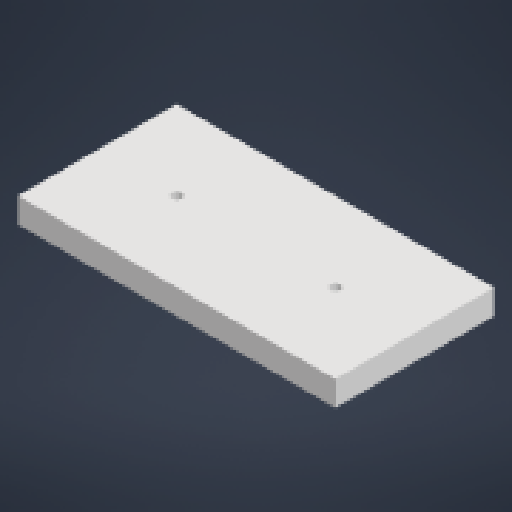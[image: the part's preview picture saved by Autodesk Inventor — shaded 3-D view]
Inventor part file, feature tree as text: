
AUTODESK INVENTOR PART (.ipt)
format: ipt  version: 2023 (Build 270158000, 158)  size: 115,712 bytes
history: native  units: in
note: dims shown in document units (in); Inventor stores cm internally (conversion verified against a paired STEP export)
features: extrude x1, sketch x1
ambient origin geometry x8: Origin, YZ Plane, XZ Plane, XY Plane, X Axis, Y Axis, Z Axis, Center Point
bodies: Solid1 (feature_tree)
feature tree (2):
  extrude  "Extrusion1"  Depth=3.0in
  sketch  "Sketch1"  dims[d0=6.0in d1=3.0in d10=1.5in d11=0.1875in d12=0.47in d13=0.0in]
